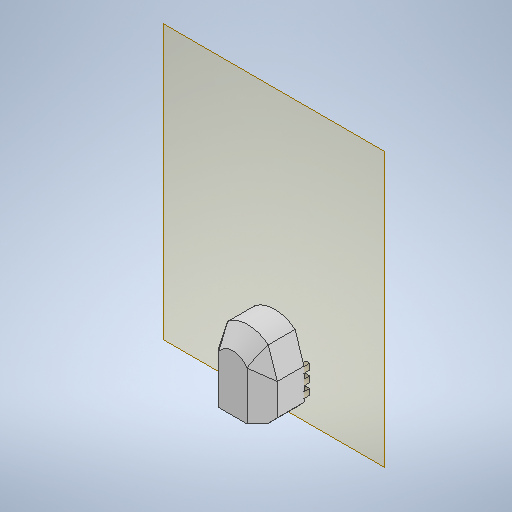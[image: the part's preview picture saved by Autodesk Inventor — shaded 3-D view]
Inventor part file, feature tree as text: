
AUTODESK INVENTOR PART (.ipt)
format: ipt  version: 2025.2 (Build 292293000, 293)  size: 359,424 bytes
history: native  units: in
note: dims shown in document units (in); Inventor stores cm internally (conversion verified against a paired STEP export)
features: reference x9, extrude x2, sketch x2, other x2, plane x1, chamfer x1, shell x1
ambient origin geometry x8: Origin, YZ Plane, XZ Plane, XY Plane, X Axis, Y Axis, Z Axis, Center Point
bodies: Solid1 (feature_tree)
feature tree (18):
  plane  "Work Plane1"
  extrude  "Extrusion1"  Depth=1.9685in TaperAngle=0.0deg
  chamfer  "Chamfer5"  Distance=0.7087in Angle=45.0deg
  shell  "Shell2"  Thickness=0.2362in
  extrude  "Extrusion3"  Depth=0.2756in
  sketch  "Sketch1"  dims[d1=0.0in d2=1.9685in d3=0.0in d31=0.7087in d32=0.125in d33=45.0deg d34=0.2362in]
  reference  "Reference1"
  reference  "Reference2"
  reference  "Reference3"
  reference  "Reference4"
  reference  "Reference5"
  reference  "Reference6"
  reference  "Reference7"
  reference  "Reference9"
  reference  "Reference10"
  sketch  "Sketch3"  dims[d47=0.1772in d48=0.2756in d49=0.1772in d50=0.2756in d51=0.1772in d52=0.2756in d53=0.1575in d54=0.2362in d55=0.2362in d56=0.0in d57=0.2717in d58=0.0in]
  other  "Thermal Camera Cover Assembly.iam"
  other  "Cylinder Slidey Bit Housing Camera only v0.2.11:1"
